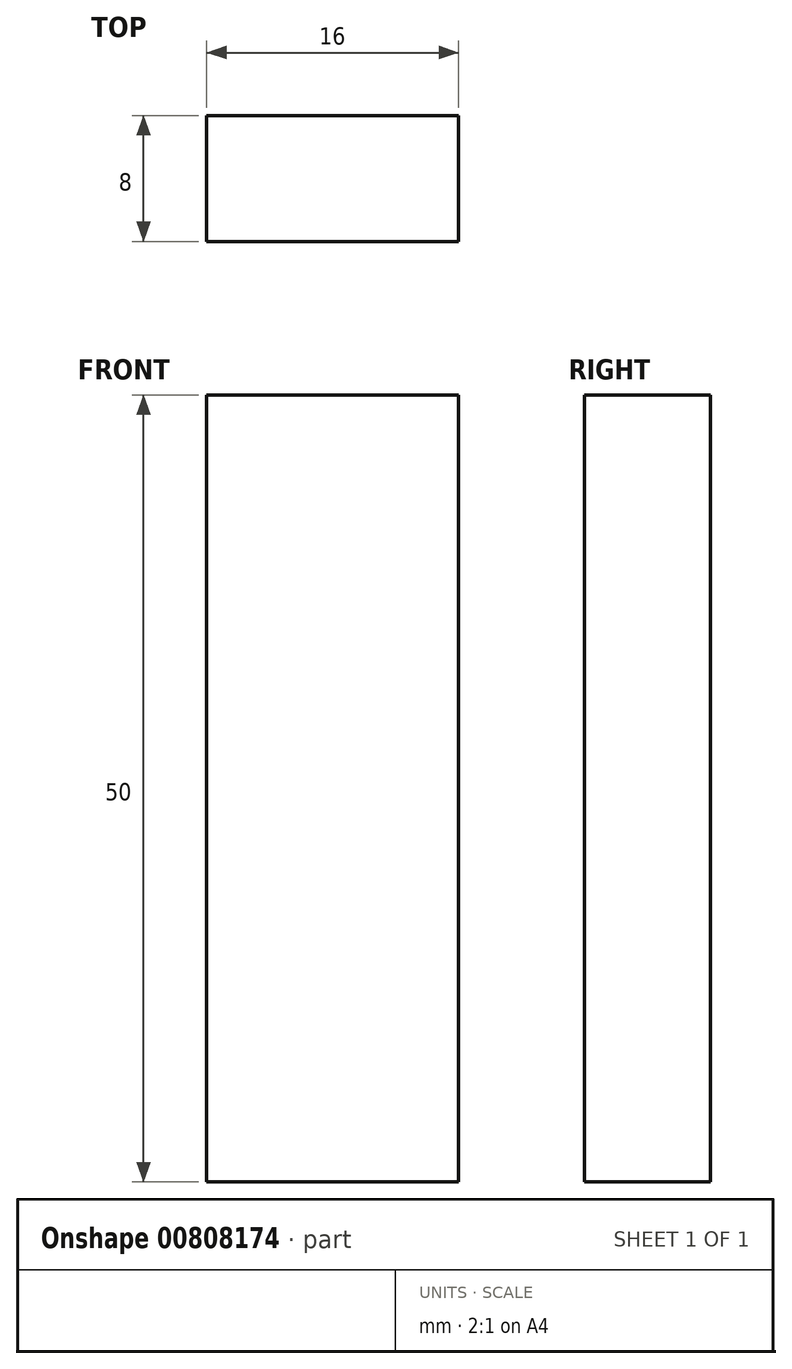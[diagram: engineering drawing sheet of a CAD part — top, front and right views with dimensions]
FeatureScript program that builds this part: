
annotation { "Feature Type Name" : "Feature", "Feature Type Description" : "" }
export const myFeature = defineFeature(function(context is Context, id is Id, definition is map)
    precondition{}
    {
        {
            var Q0;
            Q0=qCreatedBy(makeId("Front.planeOp"),FACE);
            var sketch = newSketch(context, id + "F0", { "sketchPlane" : qUnion([Q0])});
            skLineSegment(sketch, "E0.bottom", {"start": v(-25, 25) * mm, "end": v(25, 25) * mm});
            skLineSegment(sketch, "E0.top", {"start": v(-25, -25) * mm, "end": v(25, -25) * mm});
            skLineSegment(sketch, "E0.left", {"start": v(-25, 25) * mm, "end": v(-25, -25) * mm});
            skLineSegment(sketch, "E0.right", {"start": v(25, 25) * mm, "end": v(25, -25) * mm});
            skPoint(sketch, "E0.middle", {"position": v(0, 0) * mm});
            skLineSegment(sketch, "E1.bottom", {"start": v(-25, -25) * mm, "end": v(-15, -25) * mm});
            skLineSegment(sketch, "E1.top", {"start": v(-25, -15) * mm, "end": v(-15, -15) * mm});
            skLineSegment(sketch, "E1.left", {"start": v(-25, -25) * mm, "end": v(-25, -15) * mm});
            skLineSegment(sketch, "E1.right", {"start": v(-15, -25) * mm, "end": v(-15, -15) * mm});
            skLineSegment(sketch, "E2.bottom", {"start": v(-25, 25) * mm, "end": v(-15, 25) * mm});
            skLineSegment(sketch, "E2.top", {"start": v(-25, 15) * mm, "end": v(-15, 15) * mm});
            skLineSegment(sketch, "E2.left", {"start": v(-25, 25) * mm, "end": v(-25, 15) * mm});
            skLineSegment(sketch, "E2.right", {"start": v(-15, 25) * mm, "end": v(-15, 15) * mm});
            skLineSegment(sketch, "E3.bottom", {"start": v(25, 25) * mm, "end": v(15, 25) * mm});
            skLineSegment(sketch, "E3.top", {"start": v(25, 15) * mm, "end": v(15, 15) * mm});
            skLineSegment(sketch, "E3.left", {"start": v(25, 25) * mm, "end": v(25, 15) * mm});
            skLineSegment(sketch, "E3.right", {"start": v(15, 25) * mm, "end": v(15, 15) * mm});
            skLineSegment(sketch, "E4.bottom", {"start": v(25, -25) * mm, "end": v(15, -25) * mm});
            skLineSegment(sketch, "E4.top", {"start": v(25, -15) * mm, "end": v(15, -15) * mm});
            skLineSegment(sketch, "E4.left", {"start": v(25, -25) * mm, "end": v(25, -15) * mm});
            skLineSegment(sketch, "E4.right", {"start": v(15, -25) * mm, "end": v(15, -15) * mm});
            skPoint(sketch, "E5", {"position": v(-16.5, 0) * mm});
            skPoint(sketch, "E6", {"position": v(16.5, 0) * mm});
            skLineSegment(sketch, "E7.bottom", {"start": v(-25, 15) * mm, "end": v(-8, 15) * mm});
            skLineSegment(sketch, "E7.top", {"start": v(-25, -15) * mm, "end": v(-8, -15) * mm});
            skLineSegment(sketch, "E7.left", {"start": v(-25, 15) * mm, "end": v(-25, -15) * mm});
            skLineSegment(sketch, "E7.right", {"start": v(-8, 15) * mm, "end": v(-8, -15) * mm});
            skLineSegment(sketch, "E8.bottom", {"start": v(8, 15) * mm, "end": v(25, 15) * mm});
            skLineSegment(sketch, "E8.top", {"start": v(8, -15) * mm, "end": v(25, -15) * mm});
            skLineSegment(sketch, "E8.left", {"start": v(8, 15) * mm, "end": v(8, -15) * mm});
            skLineSegment(sketch, "E8.right", {"start": v(25, 15) * mm, "end": v(25, -15) * mm});
            skLineSegment(sketch, "E9", {"start": v(8, -15) * mm, "end": v(8, -25) * mm});
            skLineSegment(sketch, "E10", {"start": v(8, -25) * mm, "end": v(-15, -25) * mm});
            skLineSegment(sketch, "E11", {"start": v(-8, -15) * mm, "end": v(-8, -25) * mm});
            skLineSegment(sketch, "E12", {"start": v(-8, 15) * mm, "end": v(-8, 25) * mm});
            skLineSegment(sketch, "E13", {"start": v(8, 15) * mm, "end": v(8, 25) * mm});
            skSolve(sketch);
        }
        {
            var Q0;
            Q0=makeQuery(id+"F0.imprint","IMPRINT",FACE,{"disambiguationData":[TD([[makeQuery(id+"F0.imprint","IMPRINT",EDGE,{"derivedFrom":sQuery(id+"F0.wireOp",EDGE,"E7.right")}),1.0]])]});
            extrude(context, id + "F1", {"entities" : qUnion([Q0]), "depth" : 8 * mm, "offsetDistance" : 25 * mm});
        }
    });
